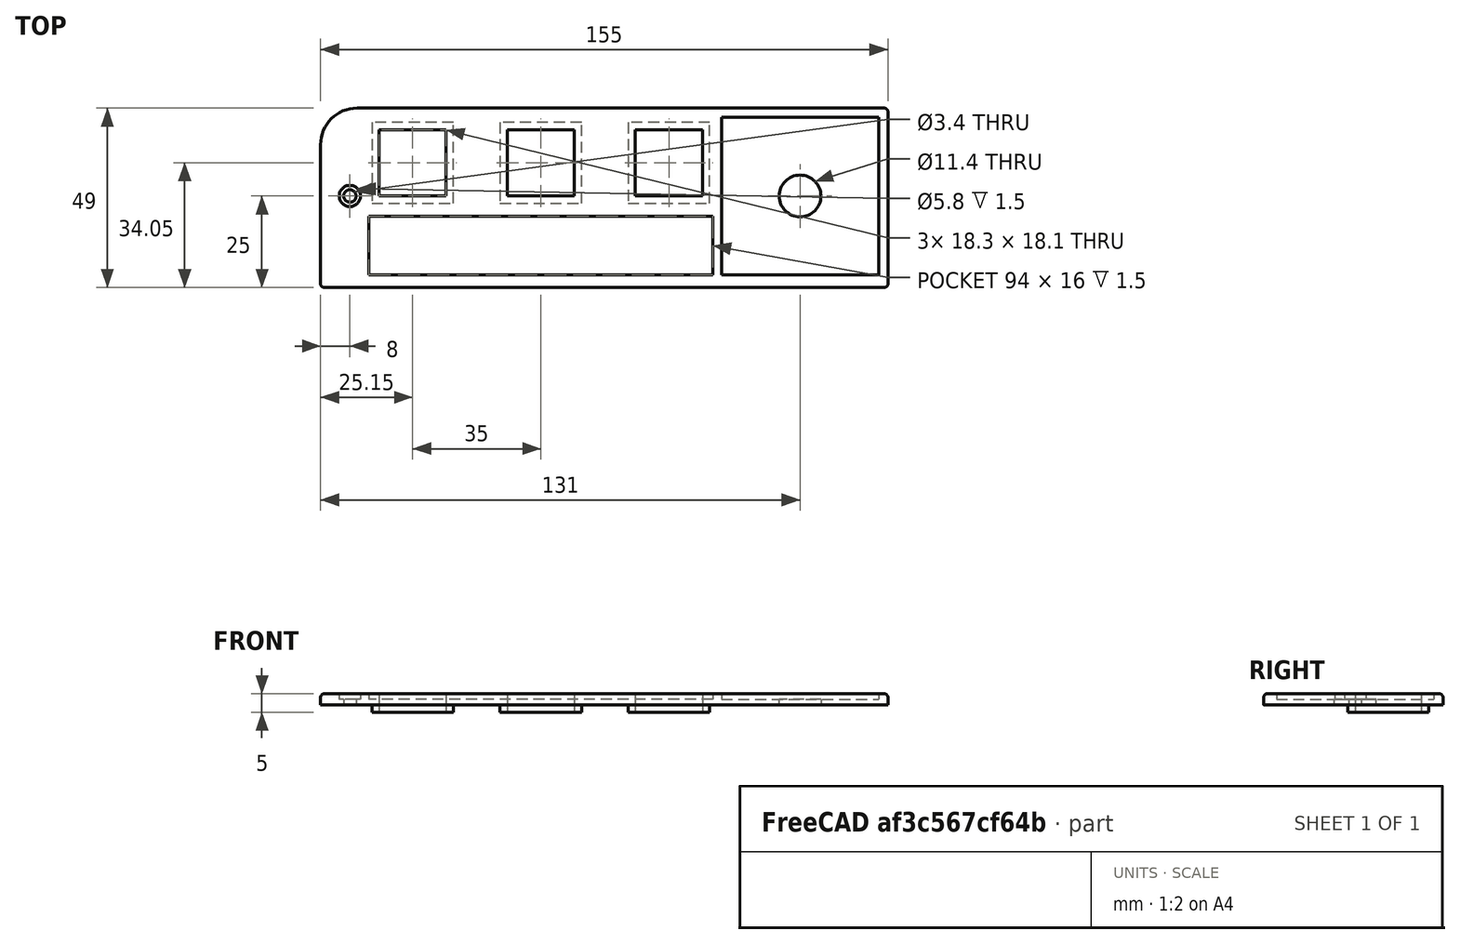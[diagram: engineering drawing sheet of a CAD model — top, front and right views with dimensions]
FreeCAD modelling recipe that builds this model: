
FCSTD DOCUMENT  (FreeCAD 0.21R33694 (Git))
Label: EnjoliveurBoutonsGauche
License: All rights reserved
LicenseURL: http://en.wikipedia.org/wiki/All_rights_reserved
objects: TechDraw::DrawViewDimension×46, Sketcher::SketchObject×7, PartDesign::Fillet×6, PartDesign::Pocket×4, TechDraw::DrawViewPart×4, TechDraw::DrawViewAnnotation×3, PartDesign::Pad×2, PartDesign::LinearPattern×2, TechDraw::DrawSVGTemplate×2, TechDraw::DrawPage×2, PartDesign::Hole×1, TechDraw::DrawViewDetail×1, TechDraw::DrawViewBalloon×1, PartDesign::Body×1
note: 36 computed .brp shape members not serialized (recipe doc carries the construction recipe); baked Part::Feature solids carry a one-line shape summary decoded from their .brp

FEATURE [Sketcher::SketchObject] Sketch  label="Main body sketch"
  FullyConstrained = true
  MapMode = 5
  Support = -> [XY_Plane]
  sketch-geometry (5):
    g0: LineSegment StartX=0 StartY=0 StartZ=0 EndX=155 EndY=0 EndZ=0
    g1: LineSegment StartX=155 StartY=0 StartZ=0 EndX=155 EndY=49 EndZ=0
    g2: LineSegment StartX=0 StartY=0 StartZ=0 EndX=0 EndY=39 EndZ=0
    g3: LineSegment StartX=155 StartY=49 StartZ=0 EndX=10 EndY=49 EndZ=0
    g4: ArcOfCircle CenterX=10 CenterY=39 CenterZ=0 NormalX=0 NormalY=0 NormalZ=1 AngleXU=0 Radius=10 StartAngle=1.5708 EndAngle=3.14159
  constraints (13):
    c: Coincident(g0,g1)
    c: Horizontal(g0)
    c: Vertical(g1)
    c: Coincident(g0,g-1)
    c: DistanceY(g1,g1) = 49
    c: DistanceX(g0,g0) = 155
    c: Coincident(g2,g0)
    c: PointOnObject(g2,g-2)
    c: Coincident(g3,g1)
    c: Horizontal(g3)
    c: Tangent(g4,g3) = -1.5708
    c: Tangent(g4,g2) = 1.5708
    c: DistanceX(g4) = 10
FEATURE [PartDesign::Pad] Pad  label="Main body"
  Direction = (0,0,1)
  Length = 3
  Length2 = 100
  Profile = -> Sketch
  Type = 0
FEATURE [Sketcher::SketchObject] Sketch001  label="Trou carre bouton sketch"
  ExternalGeometry = -> [Pad]
  FullyConstrained = true
  MapMode = 5
  Placement = pos=(0,0,3) rot=(0,0,1;0rad)
  Support = -> [Pad]
  sketch-geometry (4):
    g0: LineSegment StartX=16 StartY=43.1 StartZ=0 EndX=34.3 EndY=43.1 EndZ=0
    g1: LineSegment StartX=34.3 StartY=43.1 StartZ=0 EndX=34.3 EndY=25 EndZ=0
    g2: LineSegment StartX=34.3 StartY=25 StartZ=0 EndX=16 EndY=25 EndZ=0
    g3: LineSegment StartX=16 StartY=25 StartZ=0 EndX=16 EndY=43.1 EndZ=0
  constraints (12):
    c: Coincident(g0,g1)
    c: Coincident(g1,g2)
    c: Coincident(g2,g3)
    c: Coincident(g3,g0)
    c: Horizontal(g0)
    c: Horizontal(g2)
    c: Vertical(g1)
    c: Vertical(g3)
    c: DistanceX(g0,g0) = 18.3
    c: DistanceY(g1,g1) = 18.1
    c: DistanceY(g0,g-3) = 5.9
    c: DistanceX(g2) = 16
FEATURE [PartDesign::Pocket] Pocket  label="Trou carre bouton"
  BaseFeature = -> Pad
  Direction = (0,0,-1)
  Length = 5
  Length2 = 5
  Profile = -> Sketch001
  ReferenceAxis = -> Sketch001 [N_Axis]
  Type = 1
FEATURE [PartDesign::LinearPattern] LinearPattern  label="Trous carres boutons"
  BaseFeature = -> Pocket
  Direction = -> Sketch001 [H_Axis]
  Length = 70
  Occurrences = 3
  Originals = -> [Pocket]
FEATURE [Sketcher::SketchObject] Sketch002  label="Carre vibrato chorus sketch"
  ExternalGeometry = -> [LinearPattern]
  FullyConstrained = true
  MapMode = 5
  Placement = pos=(0,0,3) rot=(0,0,1;0rad)
  Support = -> [LinearPattern]
  sketch-geometry (4):
    g0: LineSegment StartX=109.5 StartY=46.5 StartZ=0 EndX=152.5 EndY=46.5 EndZ=0
    g1: LineSegment StartX=152.5 StartY=46.5 StartZ=0 EndX=152.5 EndY=3.5 EndZ=0
    g2: LineSegment StartX=152.5 StartY=3.5 StartZ=0 EndX=109.5 EndY=3.5 EndZ=0
    g3: LineSegment StartX=109.5 StartY=3.5 StartZ=0 EndX=109.5 EndY=46.5 EndZ=0
  constraints (12):
    c: Coincident(g0,g1)
    c: Coincident(g1,g2)
    c: Coincident(g2,g3)
    c: Coincident(g3,g0)
    c: Horizontal(g0)
    c: Horizontal(g2)
    c: Vertical(g1)
    c: Vertical(g3)
    c: DistanceX(g0,g0) = 43
    c: DistanceY(g1,g1) = 43
    c: DistanceX(g1,g-3) = 2.5
    c: DistanceY(g0,g-4) = 2.5
FEATURE [PartDesign::Pocket] Pocket001  label="Carre vibrato chorus"
  BaseFeature = -> LinearPattern
  Direction = (0,0,-1)
  Length = 1.5
  Length2 = 5
  Profile = -> Sketch002
  ReferenceAxis = -> Sketch002 [N_Axis]
  Type = 0
FEATURE [Sketcher::SketchObject] Sketch003  label="Labels boutons sketch"
  ExternalGeometry = -> [Pocket001]
  FullyConstrained = true
  MapMode = 5
  Placement = pos=(0,0,3) rot=(0,0,1;0rad)
  Support = -> [Pocket001]
  sketch-geometry (6):
    g0: LineSegment StartX=13.15 StartY=19.5 StartZ=0 EndX=107.15 EndY=19.5 EndZ=0
    g1: LineSegment StartX=107.15 StartY=19.5 StartZ=0 EndX=107.15 EndY=3.5 EndZ=0
    g2: LineSegment StartX=107.15 StartY=3.5 StartZ=0 EndX=13.15 EndY=3.5 EndZ=0
    g3: LineSegment StartX=13.15 StartY=3.5 StartZ=0 EndX=13.15 EndY=19.5 EndZ=0
    g4: LineSegment StartX=13.15 StartY=19.5 StartZ=0 EndX=16 EndY=25 EndZ=0
    g5: LineSegment StartX=104.3 StartY=25 StartZ=0 EndX=107.15 EndY=19.5 EndZ=0
  constraints (15):
    c: Coincident(g0,g1)
    c: Coincident(g1,g2)
    c: Coincident(g2,g3)
    c: Coincident(g3,g0)
    c: Horizontal(g0)
    c: Vertical(g1)
    c: Vertical(g3)
    c: DistanceX(g2,g2) = 94
    c: DistanceY(g3,g3) = 16
    c: Coincident(g4,g0)
    c: Coincident(g4,g-3)
    c: Coincident(g5,g-4)
    c: Coincident(g5,g0)
    c: Equal(g5,g4)
    c: Tangent(g2,g-5)
FEATURE [PartDesign::Pocket] Pocket002  label="Labels boutons"
  BaseFeature = -> Pocket001
  Direction = (0,0,-1)
  Length = 1.5
  Length2 = 5
  Profile = -> Sketch003
  ReferenceAxis = -> Sketch003 [N_Axis]
  Type = 0
FEATURE [Sketcher::SketchObject] Sketch004  label="Trou commutateur sketch"
  ExternalGeometry = -> [Pocket002]
  FullyConstrained = true
  MapMode = 5
  Placement = pos=(0,0,1.5) rot=(0,0,1;0rad)
  Support = -> [Pocket002]
  sketch-geometry (1):
    g0: Circle CenterX=131 CenterY=25 CenterZ=0 NormalX=0 NormalY=0 NormalZ=1 AngleXU=0 Radius=5.7
  constraints (2):
    c: Symmetric(g-3,g-4,g0)
    c: Diameter(g0) = 11.4
FEATURE [PartDesign::Pocket] Pocket003  label="Trou commutateur pocket"
  BaseFeature = -> Pocket002
  Direction = (0,0,-1)
  Length = 5
  Length2 = 5
  Profile = -> Sketch004
  ReferenceAxis = -> Sketch004 [N_Axis]
  Type = 1
FEATURE [Sketcher::SketchObject] Sketch005  label="Carre centrage bouton sketch"
  ExternalGeometry = -> [Pocket003]
  FullyConstrained = true
  MapMode = 5
  Placement = pos=(0,0,0) rot=(1,0,0;3.14159rad)
  Support = -> [Pocket003]
  sketch-geometry (8):
    g0: LineSegment StartX=16 StartY=-25 StartZ=0 EndX=34.3 EndY=-25 EndZ=0
    g1: LineSegment StartX=34.3 StartY=-25 StartZ=0 EndX=34.3 EndY=-43.1 EndZ=0
    g2: LineSegment StartX=34.3 StartY=-43.1 StartZ=0 EndX=16 EndY=-43.1 EndZ=0
    g3: LineSegment StartX=16 StartY=-43.1 StartZ=0 EndX=16 EndY=-25 EndZ=0
    g4: LineSegment StartX=14 StartY=-23 StartZ=0 EndX=36.3 EndY=-23 EndZ=0
    g5: LineSegment StartX=36.3 StartY=-23 StartZ=0 EndX=36.3 EndY=-45.1 EndZ=0
    g6: LineSegment StartX=36.3 StartY=-45.1 StartZ=0 EndX=14 EndY=-45.1 EndZ=0
    g7: LineSegment StartX=14 StartY=-45.1 StartZ=0 EndX=14 EndY=-23 EndZ=0
  constraints (21):
    c: Coincident(g0,g1)
    c: Coincident(g1,g2)
    c: Coincident(g2,g3)
    c: Coincident(g3,g0)
    c: Horizontal(g2)
    c: Vertical(g1)
    c: Coincident(g4,g5)
    c: Coincident(g5,g6)
    c: Coincident(g6,g7)
    c: Coincident(g7,g4)
    c: Horizontal(g4)
    c: Horizontal(g6)
    c: Vertical(g5)
    c: Vertical(g7)
    c: Coincident(g0,g-3)
    c: Coincident(g0,g-3)
    c: Coincident(g2,g-4)
    c: DistanceX(g6,g2) = 2
    c: DistanceX(g1,g5) = 2
    c: DistanceY(g0,g4) = 2
    c: DistanceY(g5,g1) = 2
FEATURE [PartDesign::Pad] Pad001  label="Carre centrage bouton"
  BaseFeature = -> Pocket003
  Direction = (0,0,-1)
  Length = 2
  Length2 = 10
  Profile = -> Sketch005
  ReferenceAxis = -> Sketch005 [N_Axis]
  Type = 0
FEATURE [PartDesign::LinearPattern] LinearPattern001  label="Carres centrage boutons"
  BaseFeature = -> Pad001
  Direction = -> Sketch005 [H_Axis]
  Length = 70
  Occurrences = 3
  Originals = -> [Pad001]
FEATURE [Sketcher::SketchObject] Sketch006  label="Trou fixation gauche sketch"
  ExternalGeometry = -> [LinearPattern001]
  FullyConstrained = true
  MapMode = 5
  Placement = pos=(0,0,3) rot=(0,0,1;0rad)
  Support = -> [LinearPattern001]
  sketch-geometry (2):
    g0: Circle CenterX=8 CenterY=25 CenterZ=0 NormalX=0 NormalY=0 NormalZ=1 AngleXU=0 Radius=1.5
    g1: GeomPoint X=0 Y=25 Z=0
  constraints (4):
    c: Horizontal(g-3,g0)
    c: PointOnObject(g1,g-4)
    c: Symmetric(g1,g-5,g0)
    c: Diameter(g0) = 3
FEATURE [PartDesign::Hole] Hole  label="Trou fixation gauche"
  BaseFeature = -> LinearPattern001
  CustomThreadClearance = 0
  Depth = 328.528
  DepthType = 1
  Diameter = 3.4
  DrillForDepth = false
  DrillPoint = 1
  DrillPointAngle = 118
  HoleCutCountersinkAngle = 90
  HoleCutCustomValues = false
  HoleCutDepth = 1.5
  HoleCutDiameter = 5.8
  HoleCutType = 1
  ModelThread = false
  Profile = -> Sketch006
  Tapered = false
  TaperedAngle = 90
  ThreadClass = 0
  ThreadDepth = 328.528
  ThreadDepthType = 0
  ThreadDirection = 0
  ThreadFit = 0
  ThreadSize = 9
  ThreadType = 1
  Threaded = false
  UseCustomThreadClearance = false
FEATURE [PartDesign::Fillet] Fillet
  Base = -> Hole [Edge28]
  BaseFeature = -> Hole
  Radius = 1
  SupportTransform = false
  UseAllEdges = false
FEATURE [PartDesign::Fillet] Fillet001
  Base = -> Fillet [Edge28]
  BaseFeature = -> Fillet
  Radius = 1
  SupportTransform = false
  UseAllEdges = false
FEATURE [PartDesign::Fillet] Fillet002
  Base = -> Fillet001 [Edge1]
  BaseFeature = -> Fillet001
  Radius = 1
  SupportTransform = false
  UseAllEdges = false
FEATURE [TechDraw::DrawSVGTemplate] Template
  EditableTexts = Designed_by_Name=Designed by Name; Drawing_number=Drawing number; FC-Date=Date; FC-SC=Scale; FC-SH=Sheet; FC-Title=Enjoliveur boutons gauche; Subtitle=Vues de face et de dos; Weight=Weight
  Height = 210
  Orientation = 1
  Width = 297
FEATURE [TechDraw::DrawViewPart] View  label="Vue face"
  CoarseView = false
  Direction = (0,0,1)
  Focus = 100
  HardHidden = false
  IsoCount = 0
  IsoHidden = false
  IsoVisible = false
  LockPosition = false
  Perspective = false
  Rotation = 0
  ScaleType = 0
  ScrubCount = 0
  SeamHidden = false
  SeamVisible = false
  SmoothHidden = false
  SmoothVisible = false
  Source = -> [Fillet002]
  X = 140.191
  XDirection = (1,0,0)
  Y = 167.698
FEATURE [TechDraw::DrawViewPart] View001  label="Vue dos"
  CoarseView = false
  Direction = (0,0,-1)
  Focus = 100
  HardHidden = false
  IsoCount = 0
  IsoHidden = false
  IsoVisible = false
  LockPosition = false
  Perspective = false
  Rotation = 0
  ScaleType = 0
  ScrubCount = 0
  SeamHidden = false
  SeamVisible = false
  SmoothHidden = false
  SmoothVisible = false
  Source = -> [Fillet002]
  X = 140.442
  XDirection = (-1,0,0)
  Y = 93.6691
FEATURE [TechDraw::DrawViewDimension] Dimension002
  AngleOverride = false
  Arbitrary = false
  ArbitraryTolerances = false
  EqualTolerance = true
  ExtensionAngle = 0
  FormatSpec = %.2w
  FormatSpecOverTolerance = %+.2w
  FormatSpecUnderTolerance = %+.2w
  Inverted = false
  LineAngle = 0
  LockPosition = false
  MeasureType = 1
  OverTolerance = 0
  References2D = -> [View]
  Rotation = 0
  ScaleType = 0
  TheoreticalExact = false
  Type = 1
  UnderTolerance = 0
  X = 91.1745
  Y = 21.6778
FEATURE [TechDraw::DrawViewDimension] Dimension003
  AngleOverride = false
  Arbitrary = false
  ArbitraryTolerances = false
  EqualTolerance = true
  ExtensionAngle = 0
  FormatSpec = %.2w
  FormatSpecOverTolerance = %+.2w
  FormatSpecUnderTolerance = %+.2w
  Inverted = false
  LineAngle = 0
  LockPosition = false
  MeasureType = 1
  OverTolerance = 0
  References2D = -> [View]
  Rotation = 0
  ScaleType = 0
  TheoreticalExact = false
  Type = 2
  UnderTolerance = 0
  X = 36.7305
  Y = -31.4737
FEATURE [TechDraw::DrawViewDimension] Dimension004
  AngleOverride = false
  Arbitrary = false
  ArbitraryTolerances = false
  EqualTolerance = true
  ExtensionAngle = 0
  FormatSpec = ⌀%.2w
  FormatSpecOverTolerance = %+.2w
  FormatSpecUnderTolerance = %+.2w
  Inverted = false
  LineAngle = 0
  LockPosition = false
  MeasureType = 1
  OverTolerance = 0
  References2D = -> [View]
  Rotation = 0
  ScaleType = 0
  TheoreticalExact = false
  Type = 5
  UnderTolerance = 0
  X = 69.4195
  Y = -8.56814
FEATURE [TechDraw::DrawViewDimension] Dimension005
  AngleOverride = false
  Arbitrary = false
  ArbitraryTolerances = false
  EqualTolerance = true
  ExtensionAngle = 0
  FormatSpec = %.2w
  FormatSpecOverTolerance = %+.2w
  FormatSpecUnderTolerance = %+.2w
  Inverted = false
  LineAngle = 0
  LockPosition = false
  MeasureType = 1
  OverTolerance = 0
  References2D = -> [View]
  Rotation = 0
  ScaleType = 0
  TheoreticalExact = false
  Type = 2
  UnderTolerance = 0
  X = 84.1672
  Y = -33.7381
FEATURE [TechDraw::DrawViewDimension] Dimension006
  AngleOverride = false
  Arbitrary = false
  ArbitraryTolerances = false
  EqualTolerance = true
  ExtensionAngle = 0
  FormatSpec = %.2w
  FormatSpecOverTolerance = %+.2w
  FormatSpecUnderTolerance = %+.2w
  Inverted = false
  LineAngle = 0
  LockPosition = false
  MeasureType = 1
  OverTolerance = 0
  References2D = -> [View]
  Rotation = 0
  ScaleType = 0
  TheoreticalExact = false
  Type = 1
  UnderTolerance = 0
  X = -21.8518
  Y = -35.5788
FEATURE [TechDraw::DrawViewDimension] Dimension007
  AngleOverride = false
  Arbitrary = false
  ArbitraryTolerances = false
  EqualTolerance = true
  ExtensionAngle = 0
  FormatSpec = %.2w
  FormatSpecOverTolerance = %+.2w
  FormatSpecUnderTolerance = %+.2w
  Inverted = false
  LineAngle = 0
  LockPosition = false
  MeasureType = 1
  OverTolerance = 0
  References2D = -> [View]
  Rotation = 0
  ScaleType = 0
  TheoreticalExact = false
  Type = 1
  UnderTolerance = 0
  X = -16.9764
  Y = -8.61939
FEATURE [TechDraw::DrawViewDimension] Dimension008
  AngleOverride = false
  Arbitrary = false
  ArbitraryTolerances = false
  EqualTolerance = true
  ExtensionAngle = 0
  FormatSpec = %.2w
  FormatSpecOverTolerance = %+.2w
  FormatSpecUnderTolerance = %+.2w
  Inverted = false
  LineAngle = 0
  LockPosition = false
  MeasureType = 1
  OverTolerance = 0
  References2D = -> [View]
  Rotation = 0
  ScaleType = 0
  TheoreticalExact = false
  Type = 2
  UnderTolerance = 0
  X = 14.235
  Y = -31.7605
FEATURE [TechDraw::DrawViewDimension] Dimension012
  AngleOverride = false
  Arbitrary = false
  ArbitraryTolerances = false
  EqualTolerance = true
  ExtensionAngle = 0
  FormatSpec = R%.2w
  FormatSpecOverTolerance = %+.2w
  FormatSpecUnderTolerance = %+.2w
  Inverted = false
  LineAngle = 0
  LockPosition = false
  MeasureType = 1
  OverTolerance = 0
  References2D = -> [View001]
  Rotation = 0
  ScaleType = 0
  TheoreticalExact = false
  Type = 4
  UnderTolerance = 0
  X = 83.5769
  Y = 29.2381
FEATURE [TechDraw::DrawViewDimension] Dimension013
  AngleOverride = false
  Arbitrary = false
  ArbitraryTolerances = false
  EqualTolerance = true
  ExtensionAngle = 0
  FormatSpec = %.2w
  FormatSpecOverTolerance = %+.2w
  FormatSpecUnderTolerance = %+.2w
  Inverted = false
  LineAngle = 0
  LockPosition = false
  MeasureType = 1
  OverTolerance = 0
  References2D = -> [View001]
  Rotation = 0
  ScaleType = 0
  TheoreticalExact = false
  Type = 1
  UnderTolerance = 0
  X = -17.1222
  Y = -7.29881
FEATURE [TechDraw::DrawViewDimension] Dimension014
  AngleOverride = false
  Arbitrary = false
  ArbitraryTolerances = false
  EqualTolerance = true
  ExtensionAngle = 0
  FormatSpec = %.2w
  FormatSpecOverTolerance = %+.2w
  FormatSpecUnderTolerance = %+.2w
  Inverted = false
  LineAngle = 0
  LockPosition = false
  MeasureType = 1
  OverTolerance = 0
  References2D = -> [View001]
  Rotation = 0
  ScaleType = 0
  TheoreticalExact = false
  Type = 2
  UnderTolerance = 0
  X = -39.5813
  Y = 10.3711
FEATURE [TechDraw::DrawViewDimension] Dimension015
  AngleOverride = false
  Arbitrary = false
  ArbitraryTolerances = false
  EqualTolerance = true
  ExtensionAngle = 0
  FormatSpec = %.2w
  FormatSpecOverTolerance = %+.2w
  FormatSpecUnderTolerance = %+.2w
  Inverted = false
  LineAngle = 0
  LockPosition = false
  MeasureType = 1
  OverTolerance = 0
  References2D = -> [View]
  Rotation = 0
  ScaleType = 0
  TheoreticalExact = false
  Type = 1
  UnderTolerance = 0
  X = -34.8261
  Y = 2.97613
FEATURE [TechDraw::DrawViewDimension] Dimension016
  AngleOverride = false
  Arbitrary = false
  ArbitraryTolerances = false
  EqualTolerance = true
  ExtensionAngle = 0
  FormatSpec = %.2w
  FormatSpecOverTolerance = %+.2w
  FormatSpecUnderTolerance = %+.2w
  Inverted = false
  LineAngle = 0
  LockPosition = false
  MeasureType = 1
  OverTolerance = 0
  References2D = -> [View]
  Rotation = 0
  ScaleType = 0
  TheoreticalExact = false
  Type = 1
  UnderTolerance = 0
  X = 0.173867
  Y = 2.97613
FEATURE [TechDraw::DrawViewDimension] Dimension017
  AngleOverride = false
  Arbitrary = false
  ArbitraryTolerances = false
  EqualTolerance = true
  ExtensionAngle = 0
  FormatSpec = %.2w
  FormatSpecOverTolerance = %+.2w
  FormatSpecUnderTolerance = %+.2w
  Inverted = false
  LineAngle = 0
  LockPosition = false
  MeasureType = 1
  OverTolerance = 0
  References2D = -> [View]
  Rotation = 0
  ScaleType = 0
  TheoreticalExact = false
  Type = 2
  UnderTolerance = 0
  X = -54.9884
  Y = 11.8665
FEATURE [TechDraw::DrawViewDimension] Dimension018
  AngleOverride = false
  Arbitrary = false
  ArbitraryTolerances = false
  EqualTolerance = true
  ExtensionAngle = 0
  FormatSpec = %.2w
  FormatSpecOverTolerance = %+.2w
  FormatSpecUnderTolerance = %+.2w
  Inverted = false
  LineAngle = 0
  LockPosition = false
  MeasureType = 1
  OverTolerance = 0
  References2D = -> [View]
  Rotation = 0
  ScaleType = 0
  TheoreticalExact = false
  Type = 1
  UnderTolerance = 0
  X = -16.3684
  Y = 16.2874
FEATURE [TechDraw::DrawViewDimension] Dimension019
  AngleOverride = false
  Arbitrary = false
  ArbitraryTolerances = false
  EqualTolerance = true
  ExtensionAngle = 0
  FormatSpec = %.2w
  FormatSpecOverTolerance = %+.2w
  FormatSpecUnderTolerance = %+.2w
  Inverted = false
  LineAngle = 0
  LockPosition = false
  MeasureType = 1
  OverTolerance = 0
  References2D = -> [View]
  Rotation = 0
  ScaleType = 0
  TheoreticalExact = false
  Type = 2
  UnderTolerance = 0
  X = -36.1712
  Y = 13.9698
FEATURE [TechDraw::DrawViewDimension] Dimension020
  AngleOverride = false
  Arbitrary = false
  ArbitraryTolerances = false
  EqualTolerance = true
  ExtensionAngle = 0
  FormatSpec = %.2w
  FormatSpecOverTolerance = %+.2w
  FormatSpecUnderTolerance = %+.2w
  Inverted = false
  LineAngle = 0
  LockPosition = false
  MeasureType = 1
  OverTolerance = 0
  References2D = -> [View]
  Rotation = 0
  ScaleType = 0
  TheoreticalExact = false
  Type = 1
  UnderTolerance = 0
  X = -69.4761
  Y = 19.0261
FEATURE [TechDraw::DrawViewDimension] Dimension021
  AngleOverride = false
  Arbitrary = false
  ArbitraryTolerances = false
  EqualTolerance = true
  ExtensionAngle = 0
  FormatSpec = %.2w
  FormatSpecOverTolerance = %+.2w
  FormatSpecUnderTolerance = %+.2w
  Inverted = false
  LineAngle = 0
  LockPosition = false
  MeasureType = 1
  OverTolerance = 0
  References2D = -> [View001]
  Rotation = 0
  ScaleType = 0
  TheoreticalExact = false
  Type = 2
  UnderTolerance = 0
  X = 13.8416
  Y = 11.8163
FEATURE [TechDraw::DrawViewDimension] Dimension022
  AngleOverride = false
  Arbitrary = false
  ArbitraryTolerances = false
  EqualTolerance = true
  ExtensionAngle = 0
  FormatSpec = %.2w
  FormatSpecOverTolerance = %+.2w
  FormatSpecUnderTolerance = %+.2w
  Inverted = false
  LineAngle = 0
  LockPosition = false
  MeasureType = 1
  OverTolerance = 0
  References2D = -> [View001]
  Rotation = 0
  ScaleType = 0
  TheoreticalExact = false
  Type = 1
  UnderTolerance = 0
  X = 52.7458
  Y = 12.8382
FEATURE [TechDraw::DrawViewAnnotation] Annotation
  Font = osifont
  LineSpace = 80
  LockPosition = false
  MaxWidth = -1
  Rotation = 0
  ScaleType = 0
  Text = 1 : Vis à tôle - Tête cylindrique crucif. M 2.2 x 6.4 Zingué
  TextSize = 5
  TextStyle = 0
  X = 76.1545
  Y = 31.0143
FEATURE [TechDraw::DrawViewDetail] Detail  label="Detail trou fixation"
  AnchorPoint = (-69.5,0.34,0)
  BaseView = -> View
  CoarseView = false
  Direction = (0,0,1)
  Focus = 100
  HardHidden = false
  IsoCount = 0
  IsoHidden = false
  IsoVisible = false
  LockPosition = false
  Perspective = false
  Radius = 7
  Reference = Trou fixation
  Rotation = 0
  Scale = 3
  ScaleType = 2
  ScrubCount = 0
  SeamHidden = false
  SeamVisible = false
  SmoothHidden = false
  SmoothVisible = false
  Source = -> [Fillet002]
  X = 31.1244
  XDirection = (1,0,0)
  Y = 145.737
FEATURE [TechDraw::DrawViewDimension] Dimension024
  AngleOverride = false
  Arbitrary = false
  ArbitraryTolerances = false
  EqualTolerance = true
  ExtensionAngle = 0
  FormatSpec = ⌀%.2w
  FormatSpecOverTolerance = %+.2w
  FormatSpecUnderTolerance = %+.2w
  Inverted = false
  LineAngle = 0
  LockPosition = false
  MeasureType = 1
  OverTolerance = 0
  References2D = -> [Detail]
  Rotation = 0
  ScaleType = 0
  TheoreticalExact = false
  Type = 5
  UnderTolerance = 0
  X = 13.125
  Y = 13.8542
FEATURE [TechDraw::DrawSVGTemplate] Template001
  EditableTexts = Designed_by_Name=Designed by Name; Drawing_number=Drawing number; FC-Date=Date; FC-SC=Scale; FC-SH=Sheet; FC-Title=Enjoliveur boutons gauche; Subtitle=Vues de profil; Weight=Weight
  Height = 210
  Orientation = 1
  Width = 297
FEATURE [TechDraw::DrawViewPart] View002
  CoarseView = true
  Direction = (0,-1,0)
  Focus = 100
  HardHidden = true
  IsoCount = 0
  IsoHidden = false
  IsoVisible = true
  LockPosition = false
  Perspective = false
  Rotation = 0
  Scale = 1.7
  ScaleType = 2
  ScrubCount = 0
  SeamHidden = false
  SeamVisible = true
  SmoothHidden = true
  SmoothVisible = false
  Source = -> [Fillet002]
  X = 147.995
  XDirection = (1,0,0)
  Y = 165.467
FEATURE [TechDraw::DrawViewPart] View003
  CoarseView = false
  Direction = (1,0,0)
  Focus = 100
  HardHidden = true
  IsoCount = 0
  IsoHidden = false
  IsoVisible = false
  LockPosition = false
  Perspective = false
  Rotation = 0
  Scale = 5
  ScaleType = 2
  ScrubCount = 0
  SeamHidden = true
  SeamVisible = false
  SmoothHidden = false
  SmoothVisible = false
  Source = -> [Fillet002]
  X = 145.171
  XDirection = (0,1,0)
  Y = 94.7532
FEATURE [TechDraw::DrawViewDimension] Dimension025
  AngleOverride = false
  Arbitrary = false
  ArbitraryTolerances = false
  EqualTolerance = true
  ExtensionAngle = 0
  FormatSpec = %.2w
  FormatSpecOverTolerance = %+.2w
  FormatSpecUnderTolerance = %+.2w
  Inverted = false
  LineAngle = 0
  LockPosition = false
  MeasureType = 1
  OverTolerance = 0
  References2D = -> [View003]
  Rotation = 0
  ScaleType = 0
  TheoreticalExact = false
  Type = 2
  UnderTolerance = 0
  X = -22.5595
  Y = 29.8643
FEATURE [TechDraw::DrawViewDimension] Dimension026
  AngleOverride = false
  Arbitrary = false
  ArbitraryTolerances = false
  EqualTolerance = true
  ExtensionAngle = 0
  FormatSpec = %.2w
  FormatSpecOverTolerance = %+.2w
  FormatSpecUnderTolerance = %+.2w
  Inverted = false
  LineAngle = 0
  LockPosition = false
  MeasureType = 1
  OverTolerance = 0
  References2D = -> [View003]
  Rotation = 0
  ScaleType = 0
  TheoreticalExact = false
  Type = 2
  UnderTolerance = 0
  X = 60.163
  Y = 29.5517
FEATURE [TechDraw::DrawViewDimension] Dimension027
  AngleOverride = false
  Arbitrary = false
  ArbitraryTolerances = false
  EqualTolerance = true
  ExtensionAngle = 0
  FormatSpec = %.2w
  FormatSpecOverTolerance = %+.2w
  FormatSpecUnderTolerance = %+.2w
  Inverted = false
  LineAngle = 0
  LockPosition = false
  MeasureType = 1
  OverTolerance = 0
  References2D = -> [View]
  Rotation = 0
  ScaleType = 0
  TheoreticalExact = false
  Type = 2
  UnderTolerance = 0
  X = -39.764
  Y = -33.4312
FEATURE [TechDraw::DrawViewDimension] Dimension028
  AngleOverride = false
  Arbitrary = false
  ArbitraryTolerances = false
  EqualTolerance = true
  ExtensionAngle = 0
  FormatSpec = %.2w
  FormatSpecOverTolerance = %+.2w
  FormatSpecUnderTolerance = %+.2w
  Inverted = false
  LineAngle = 0
  LockPosition = false
  MeasureType = 1
  OverTolerance = 0
  References2D = -> [View001]
  Rotation = 0
  ScaleType = 0
  TheoreticalExact = false
  Type = 2
  UnderTolerance = 0
  X = -95.2153
  Y = 2.01389
FEATURE [TechDraw::DrawViewDimension] Dimension
  AngleOverride = false
  Arbitrary = false
  ArbitraryTolerances = false
  EqualTolerance = true
  ExtensionAngle = 0
  FormatSpec = %.2w
  FormatSpecOverTolerance = %+.2w
  FormatSpecUnderTolerance = %+.2w
  Inverted = false
  LineAngle = 0
  LockPosition = false
  MeasureType = 1
  OverTolerance = 0
  References2D = -> [View001]
  Rotation = 0
  ScaleType = 0
  TheoreticalExact = false
  Type = 1
  UnderTolerance = 0
  X = -1.94444
  Y = -25.6181
FEATURE [TechDraw::DrawViewDimension] Dimension029
  AngleOverride = false
  Arbitrary = false
  ArbitraryTolerances = false
  EqualTolerance = true
  ExtensionAngle = 0
  FormatSpec = %.2w
  FormatSpecOverTolerance = %+.2w
  FormatSpecUnderTolerance = %+.2w
  Inverted = false
  LineAngle = 0
  LockPosition = false
  MeasureType = 1
  OverTolerance = 0
  References2D = -> [View]
  Rotation = 0
  ScaleType = 0
  TheoreticalExact = false
  Type = 1
  UnderTolerance = 0
  X = 91.8056
  Y = 12.5903
FEATURE [TechDraw::DrawViewDimension] Dimension030
  AngleOverride = false
  Arbitrary = false
  ArbitraryTolerances = false
  EqualTolerance = true
  ExtensionAngle = 0
  FormatSpec = %.2w
  FormatSpecOverTolerance = %+.2w
  FormatSpecUnderTolerance = %+.2w
  Inverted = false
  LineAngle = 0
  LockPosition = false
  MeasureType = 1
  OverTolerance = 0
  References2D = -> [View]
  Rotation = 0
  ScaleType = 0
  TheoreticalExact = false
  Type = 1
  UnderTolerance = 0
  X = -54.1542
  Y = -26.5208
FEATURE [TechDraw::DrawViewDimension] Dimension031
  AngleOverride = false
  Arbitrary = false
  ArbitraryTolerances = false
  EqualTolerance = true
  ExtensionAngle = 0
  FormatSpec = %.2w
  FormatSpecOverTolerance = %+.2w
  FormatSpecUnderTolerance = %+.2w
  Inverted = false
  LineAngle = 0
  LockPosition = false
  MeasureType = 1
  OverTolerance = 0
  References2D = -> [View001]
  Rotation = 0
  ScaleType = 0
  TheoreticalExact = false
  Type = 2
  UnderTolerance = 0
  X = 32.625
  Y = -11.4167
FEATURE [TechDraw::DrawViewDimension] Dimension032
  AngleOverride = false
  Arbitrary = false
  ArbitraryTolerances = false
  EqualTolerance = true
  ExtensionAngle = 0
  FormatSpec = %.2w
  FormatSpecOverTolerance = %+.2w
  FormatSpecUnderTolerance = %+.2w
  Inverted = false
  LineAngle = 0
  LockPosition = false
  MeasureType = 1
  OverTolerance = 0
  References2D = -> [View001]
  Rotation = 0
  ScaleType = 0
  TheoreticalExact = false
  Type = 1
  UnderTolerance = 0
  X = 15.95
  Y = -7.20833
FEATURE [TechDraw::DrawViewAnnotation] Annotation001
  Font = osifont
  LineSpace = 80
  LockPosition = false
  MaxWidth = -1
  Rotation = 0
  ScaleType = 0
  Text = échelle = 170/100
  TextSize = 5
  TextStyle = 0
  X = 260.299
  Y = 151.079
FEATURE [TechDraw::DrawViewAnnotation] Annotation002
  Font = osifont
  LineSpace = 80
  LockPosition = false
  MaxWidth = -1
  Rotation = 0
  ScaleType = 0
  Text = échelle = 500/100
  TextSize = 5
  TextStyle = 0
  X = 42.9964
  Y = 77.0504
FEATURE [TechDraw::DrawViewDimension] Dimension033
  AngleOverride = false
  Arbitrary = false
  ArbitraryTolerances = false
  EqualTolerance = true
  ExtensionAngle = 0
  FormatSpec = %.2w
  FormatSpecOverTolerance = %+.2w
  FormatSpecUnderTolerance = %+.2w
  Inverted = false
  LineAngle = 0
  LockPosition = false
  MeasureType = 1
  OverTolerance = 0
  References2D = -> [View003]
  Rotation = 0
  ScaleType = 0
  TheoreticalExact = false
  Type = 2
  UnderTolerance = 0
  X = -98.6078
  Y = 30.2598
FEATURE [TechDraw::DrawViewDimension] Dimension034
  AngleOverride = false
  Arbitrary = false
  ArbitraryTolerances = false
  EqualTolerance = true
  ExtensionAngle = 0
  FormatSpec = %.2w
  FormatSpecOverTolerance = %+.2w
  FormatSpecUnderTolerance = %+.2w
  Inverted = false
  LineAngle = 0
  LockPosition = false
  MeasureType = 1
  OverTolerance = 0
  References2D = -> [View003]
  Rotation = 0
  ScaleType = 0
  TheoreticalExact = false
  Type = 1
  UnderTolerance = 0
  X = -67.097
  Y = -2.24921
FEATURE [TechDraw::DrawViewDimension] Dimension035
  AngleOverride = false
  Arbitrary = false
  ArbitraryTolerances = false
  EqualTolerance = true
  ExtensionAngle = 0
  FormatSpec = %.2w
  FormatSpecOverTolerance = %+.2w
  FormatSpecUnderTolerance = %+.2w
  Inverted = false
  LineAngle = 0
  LockPosition = false
  MeasureType = 1
  OverTolerance = 0
  References2D = -> [View003]
  Rotation = 0
  ScaleType = 0
  TheoreticalExact = false
  Type = 1
  UnderTolerance = 0
  X = 48.4228
  Y = -25.5046
FEATURE [TechDraw::DrawViewDimension] Dimension036
  AngleOverride = false
  Arbitrary = false
  ArbitraryTolerances = false
  EqualTolerance = true
  ExtensionAngle = 0
  FormatSpec = R%.2w
  FormatSpecOverTolerance = %+.2w
  FormatSpecUnderTolerance = %+.2w
  Inverted = false
  LineAngle = 0
  LockPosition = false
  MeasureType = 1
  OverTolerance = 0
  References2D = -> [View003]
  Rotation = 0
  ScaleType = 0
  TheoreticalExact = false
  Type = 4
  UnderTolerance = 0
  X = 127.41
  Y = 22.4101
FEATURE [TechDraw::DrawViewDimension] Dimension037
  AngleOverride = false
  Arbitrary = false
  ArbitraryTolerances = false
  EqualTolerance = true
  ExtensionAngle = 0
  FormatSpec = %.2w
  FormatSpecOverTolerance = %+.2w
  FormatSpecUnderTolerance = %+.2w
  Inverted = false
  LineAngle = 0
  LockPosition = false
  MeasureType = 1
  OverTolerance = 0
  References2D = -> [View003]
  Rotation = 0
  ScaleType = 0
  TheoreticalExact = false
  Type = 1
  UnderTolerance = 0
  X = 2.18362
  Y = 43.1105
FEATURE [TechDraw::DrawViewDimension] Dimension038
  AngleOverride = false
  Arbitrary = false
  ArbitraryTolerances = false
  EqualTolerance = true
  ExtensionAngle = 0
  FormatSpec = %.2w
  FormatSpecOverTolerance = %+.2w
  FormatSpecUnderTolerance = %+.2w
  Inverted = false
  LineAngle = 0
  LockPosition = false
  MeasureType = 1
  OverTolerance = 0
  References2D = -> [View003]
  Rotation = 0
  ScaleType = 0
  TheoreticalExact = false
  Type = 1
  UnderTolerance = 0
  X = -113.833
  Y = -2.19525
FEATURE [TechDraw::DrawViewDimension] Dimension039
  AngleOverride = false
  Arbitrary = false
  ArbitraryTolerances = false
  EqualTolerance = true
  ExtensionAngle = 0
  FormatSpec = %.2w
  FormatSpecOverTolerance = %+.2w
  FormatSpecUnderTolerance = %+.2w
  Inverted = false
  LineAngle = 0
  LockPosition = false
  MeasureType = 1
  OverTolerance = 0
  References2D = -> [View003]
  Rotation = 0
  ScaleType = 0
  TheoreticalExact = false
  Type = 1
  UnderTolerance = 0
  X = 112.667
  Y = -3.41827
FEATURE [TechDraw::DrawViewDimension] Dimension040
  AngleOverride = false
  Arbitrary = false
  ArbitraryTolerances = false
  EqualTolerance = true
  ExtensionAngle = 0
  FormatSpec = %.2w
  FormatSpecOverTolerance = %+.2w
  FormatSpecUnderTolerance = %+.2w
  Inverted = false
  LineAngle = 0
  LockPosition = false
  MeasureType = 1
  OverTolerance = 0
  References2D = -> [View003]
  Rotation = 0
  ScaleType = 0
  TheoreticalExact = false
  Type = 1
  UnderTolerance = 0
  X = 112.703
  Y = -12.2312
FEATURE [TechDraw::DrawViewDimension] Dimension041
  AngleOverride = false
  Arbitrary = false
  ArbitraryTolerances = false
  EqualTolerance = true
  ExtensionAngle = 0
  FormatSpec = %.2w
  FormatSpecOverTolerance = %+.2w
  FormatSpecUnderTolerance = %+.2w
  Inverted = false
  LineAngle = 0
  LockPosition = false
  MeasureType = 1
  OverTolerance = 0
  References2D = -> [View003]
  Rotation = 0
  ScaleType = 0
  TheoreticalExact = false
  Type = 1
  UnderTolerance = 0
  X = 48.4228
  Y = -16.7636
FEATURE [TechDraw::DrawViewDimension] Dimension042
  AngleOverride = false
  Arbitrary = false
  ArbitraryTolerances = false
  EqualTolerance = true
  ExtensionAngle = 0
  FormatSpec = %.2w
  FormatSpecOverTolerance = %+.2w
  FormatSpecUnderTolerance = %+.2w
  Inverted = false
  LineAngle = 0
  LockPosition = false
  MeasureType = 1
  OverTolerance = 0
  References2D = -> [View003]
  Rotation = 0
  ScaleType = 0
  TheoreticalExact = false
  Type = 1
  UnderTolerance = 0
  X = -19.9567
  Y = -16.5118
FEATURE [TechDraw::DrawViewDimension] Dimension043
  AngleOverride = false
  Arbitrary = false
  ArbitraryTolerances = false
  EqualTolerance = true
  ExtensionAngle = 0
  FormatSpec = %.2w
  FormatSpecOverTolerance = %+.2w
  FormatSpecUnderTolerance = %+.2w
  Inverted = false
  LineAngle = 0
  LockPosition = false
  MeasureType = 1
  OverTolerance = 0
  References2D = -> [View001]
  Rotation = 0
  ScaleType = 0
  TheoreticalExact = false
  Type = 2
  UnderTolerance = 0
  X = 88.8002
  Y = -10.0746
FEATURE [TechDraw::DrawViewDimension] Dimension044
  AngleOverride = false
  Arbitrary = false
  ArbitraryTolerances = false
  EqualTolerance = true
  ExtensionAngle = 0
  FormatSpec = %.2w
  FormatSpecOverTolerance = %+.2w
  FormatSpecUnderTolerance = %+.2w
  Inverted = false
  LineAngle = 0
  LockPosition = false
  MeasureType = 1
  OverTolerance = 0
  References2D = -> [View001]
  Rotation = 0
  ScaleType = 0
  TheoreticalExact = false
  Type = 2
  UnderTolerance = 0
  X = -85.2691
  Y = -9.1169
FEATURE [TechDraw::DrawViewDimension] Dimension045
  AngleOverride = false
  Arbitrary = false
  ArbitraryTolerances = false
  EqualTolerance = true
  ExtensionAngle = 0
  FormatSpec = %.2w
  FormatSpecOverTolerance = %+.2w
  FormatSpecUnderTolerance = %+.2w
  Inverted = false
  LineAngle = 0
  LockPosition = false
  MeasureType = 1
  OverTolerance = 0
  References2D = -> [View001]
  Rotation = 0
  ScaleType = 0
  TheoreticalExact = false
  Type = 1
  UnderTolerance = 0
  X = 85.7645
  Y = 15.9245
FEATURE [TechDraw::DrawViewDimension] Dimension046
  AngleOverride = false
  Arbitrary = false
  ArbitraryTolerances = false
  EqualTolerance = true
  ExtensionAngle = 0
  FormatSpec = %.2w
  FormatSpecOverTolerance = %+.2w
  FormatSpecUnderTolerance = %+.2w
  Inverted = false
  LineAngle = 0
  LockPosition = false
  MeasureType = 1
  OverTolerance = 0
  References2D = -> [View001]
  Rotation = 0
  ScaleType = 0
  TheoreticalExact = false
  Type = 1
  UnderTolerance = 0
  X = -65.3084
  Y = 18.5437
FEATURE [TechDraw::DrawViewDimension] Dimension047
  AngleOverride = false
  Arbitrary = false
  ArbitraryTolerances = false
  EqualTolerance = true
  ExtensionAngle = 0
  FormatSpec = %.2w
  FormatSpecOverTolerance = %+.2w
  FormatSpecUnderTolerance = %+.2w
  Inverted = false
  LineAngle = 0
  LockPosition = false
  MeasureType = 1
  OverTolerance = 0
  References2D = -> [View003]
  Rotation = 0
  ScaleType = 0
  TheoreticalExact = false
  Type = 1
  UnderTolerance = 0
  X = 1.7446
  Y = 31.5858
FEATURE [TechDraw::DrawViewDimension] Dimension048
  AngleOverride = false
  Arbitrary = false
  ArbitraryTolerances = false
  EqualTolerance = true
  ExtensionAngle = 0
  FormatSpec = %.2w
  FormatSpecOverTolerance = %+.2w
  FormatSpecUnderTolerance = %+.2w
  Inverted = false
  LineAngle = 0
  LockPosition = false
  MeasureType = 1
  OverTolerance = 0
  References2D = -> [View003]
  Rotation = 0
  ScaleType = 0
  TheoreticalExact = false
  Type = 1
  UnderTolerance = 0
  X = 2.7518
  Y = 24.0966
FEATURE [TechDraw::DrawViewDimension] Dimension049
  AngleOverride = false
  Arbitrary = false
  ArbitraryTolerances = false
  EqualTolerance = true
  ExtensionAngle = 0
  FormatSpec = %.2w
  FormatSpecOverTolerance = %+.2w
  FormatSpecUnderTolerance = %+.2w
  Inverted = false
  LineAngle = 0
  LockPosition = false
  MeasureType = 1
  OverTolerance = 0
  References2D = -> [View003]
  Rotation = 0
  ScaleType = 0
  TheoreticalExact = false
  Type = 2
  UnderTolerance = 0
  X = 21.8058
  Y = 28.093
FEATURE [TechDraw::DrawPage] Page001  label="Page vues de profil"
  KeepUpdated = true
  NextBalloonIndex = 1
  ProjectionType = 0
  Template = -> Template001
  Views = -> [View002,View003,Dimension025,Dimension026,Annotation001,Annotation002,Dimension033,Dimension034,Dimension035,Dimension036,Dimension037,Dimension038,Dimension039,Dimension040,Dimension041,Dimension042,Dimension047,Dimension048,Dimension049]
FEATURE [TechDraw::DrawViewBalloon] Balloon
  BubbleShape = 0
  EndType = 0
  EndTypeScale = 1
  KinkLength = 5
  LockPosition = false
  OriginX = -71.8
  OriginY = 0.5
  Rotation = 0
  ScaleType = 0
  ShapeScale = 1
  SourceView = -> View
  Text = 1
  TextWrapLen = -1
  X = -103.997
  Y = 16.5094
FEATURE [TechDraw::DrawViewDimension] Dimension050
  AngleOverride = false
  Arbitrary = false
  ArbitraryTolerances = false
  EqualTolerance = true
  ExtensionAngle = 0
  FormatSpec = ⌀%.2w
  FormatSpecOverTolerance = %+.2w
  FormatSpecUnderTolerance = %+.2w
  Inverted = false
  LineAngle = 0
  LockPosition = false
  MeasureType = 1
  OverTolerance = 0
  References2D = -> [Detail]
  Rotation = 0
  ScaleType = 0
  TheoreticalExact = false
  Type = 5
  UnderTolerance = 0
  X = 0
  Y = 0
FEATURE [TechDraw::DrawPage] Page  label="Page vues face et dos"
  KeepUpdated = true
  NextBalloonIndex = 2
  ProjectionType = 0
  Template = -> Template
  Views = -> [View,View001,Dimension002,Dimension003,Dimension004,Dimension005,Dimension006,Dimension007,Dimension008,Dimension012,Dimension013,Dimension014,Dimension015,Dimension016,Dimension017,Dimension018,Dimension019,Dimension020,Dimension021,Dimension022,Annotation,Detail,Dimension024,Dimension027,Dimension028,Dimension,Dimension029,Dimension030,Dimension031,Dimension032,Dimension043,Dimension044,+4 more]
FEATURE [PartDesign::Fillet] Fillet003
  Base = -> Hole [Edge28]
  BaseFeature = -> Hole
  Radius = 1
  SupportTransform = false
  UseAllEdges = false
FEATURE [PartDesign::Fillet] Fillet004
  Base = -> Fillet003 [Edge4]
  BaseFeature = -> Fillet003
  Radius = 1
  SupportTransform = false
  UseAllEdges = false
FEATURE [PartDesign::Fillet] Fillet005
  Base = -> Fillet004 [Edge26]
  BaseFeature = -> Fillet004
  Radius = 1
  SupportTransform = false
  UseAllEdges = false
FEATURE [PartDesign::Body] Body  label="Body part1"
  Group = -> [Sketch,Pad,Sketch001,Pocket,LinearPattern,Sketch002,Pocket001,Sketch003,Pocket002,Sketch004,Pocket003,Sketch005,Pad001,LinearPattern001,Sketch006,Hole,Fillet,Fillet001,Fillet002,Fillet003,Fillet004,Fillet005]
  Origin = -> Origin
  Tip = -> Fillet005
